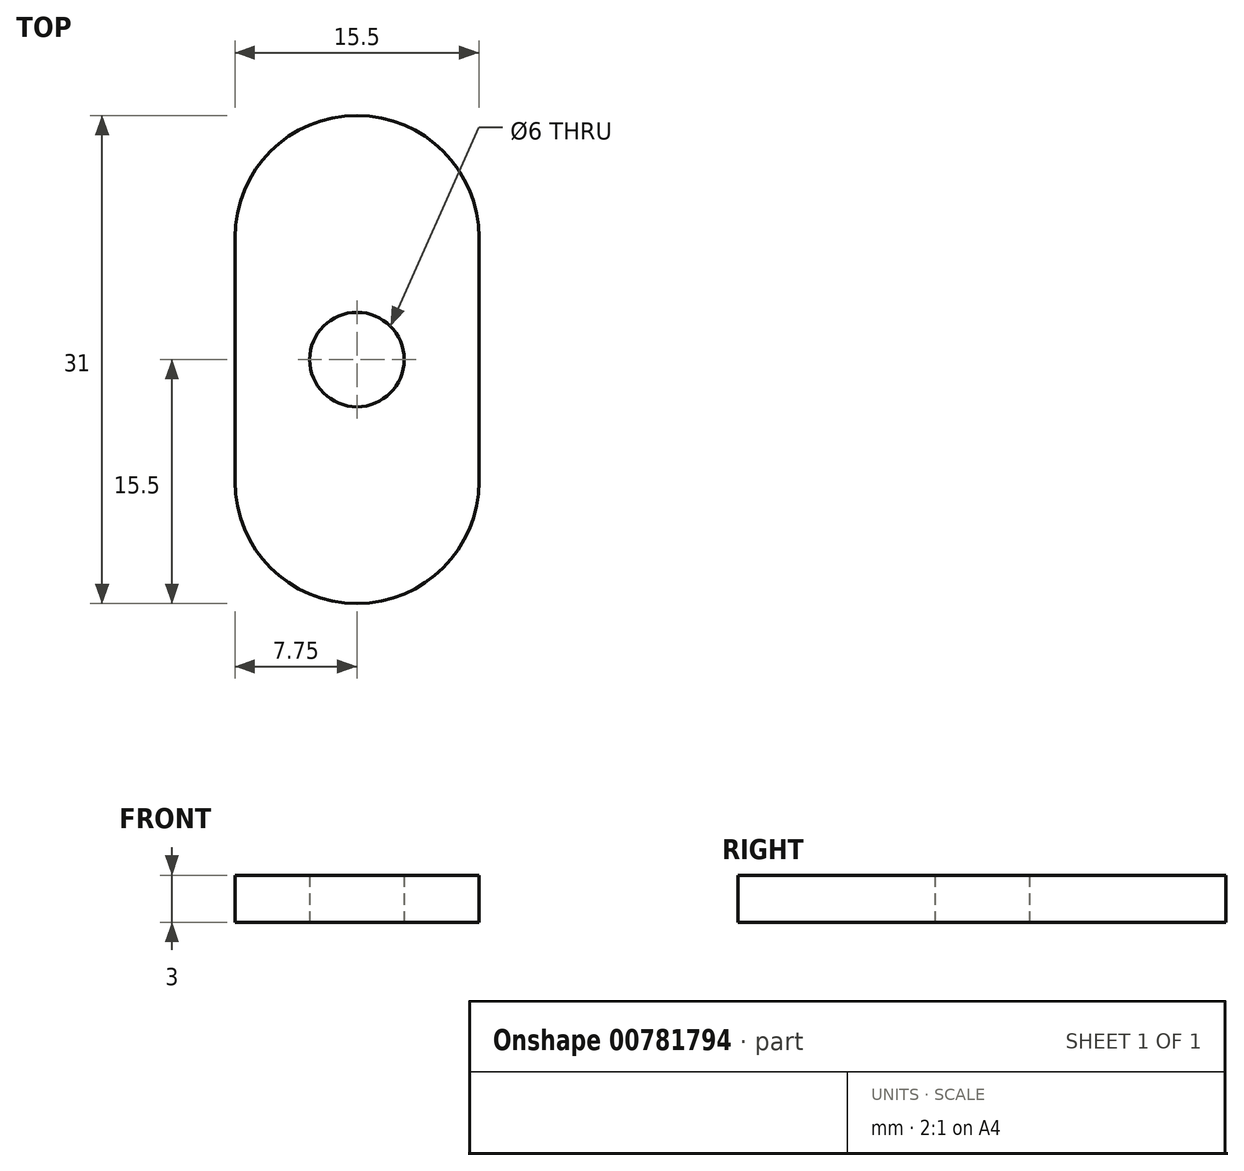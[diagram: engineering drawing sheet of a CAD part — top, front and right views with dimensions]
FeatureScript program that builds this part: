
annotation { "Feature Type Name" : "Feature", "Feature Type Description" : "" }
export const myFeature = defineFeature(function(context is Context, id is Id, definition is map)
    precondition{}
    {
        {
            var Q0;
            Q0=qCreatedBy(makeId("Top.planeOp"),FACE);
            var sketch = newSketch(context, id + "F0", { "sketchPlane" : qUnion([Q0])});
            skLineSegment(sketch, "E0.left", {"start": v(7.75, -7.75) * mm, "end": v(7.75, 7.75) * mm});
            skLineSegment(sketch, "E0.right", {"start": v(-7.75, -7.75) * mm, "end": v(-7.75, 7.75) * mm});
            skPoint(sketch, "E0.middle", {"position": v(0, 0) * mm});
            skArc(sketch, "E1", {"start": v(-7.75, 7.75) * mm, "mid": v(0, 15.5) * mm, "end": v(7.75, 7.75) * mm});
            skArc(sketch, "E2", {"start": v(7.75, -7.75) * mm, "mid": v(0, -15.5) * mm, "end": v(-7.75, -7.75) * mm});
            skCircle(sketch, "E3", {"center": v(0, 0) * mm, "radius": 3 * mm});
            skSolve(sketch);
        }
        {
            var Q0;
            Q0 = qSketchRegion(id + "F0", true);
            extrude(context, id + "F1", {"entities" : qUnion([Q0]), "endBound" : BoundingType.SYMMETRIC, "depth" : 3 * mm, "offsetDistance" : 25 * mm});
        }
    });
